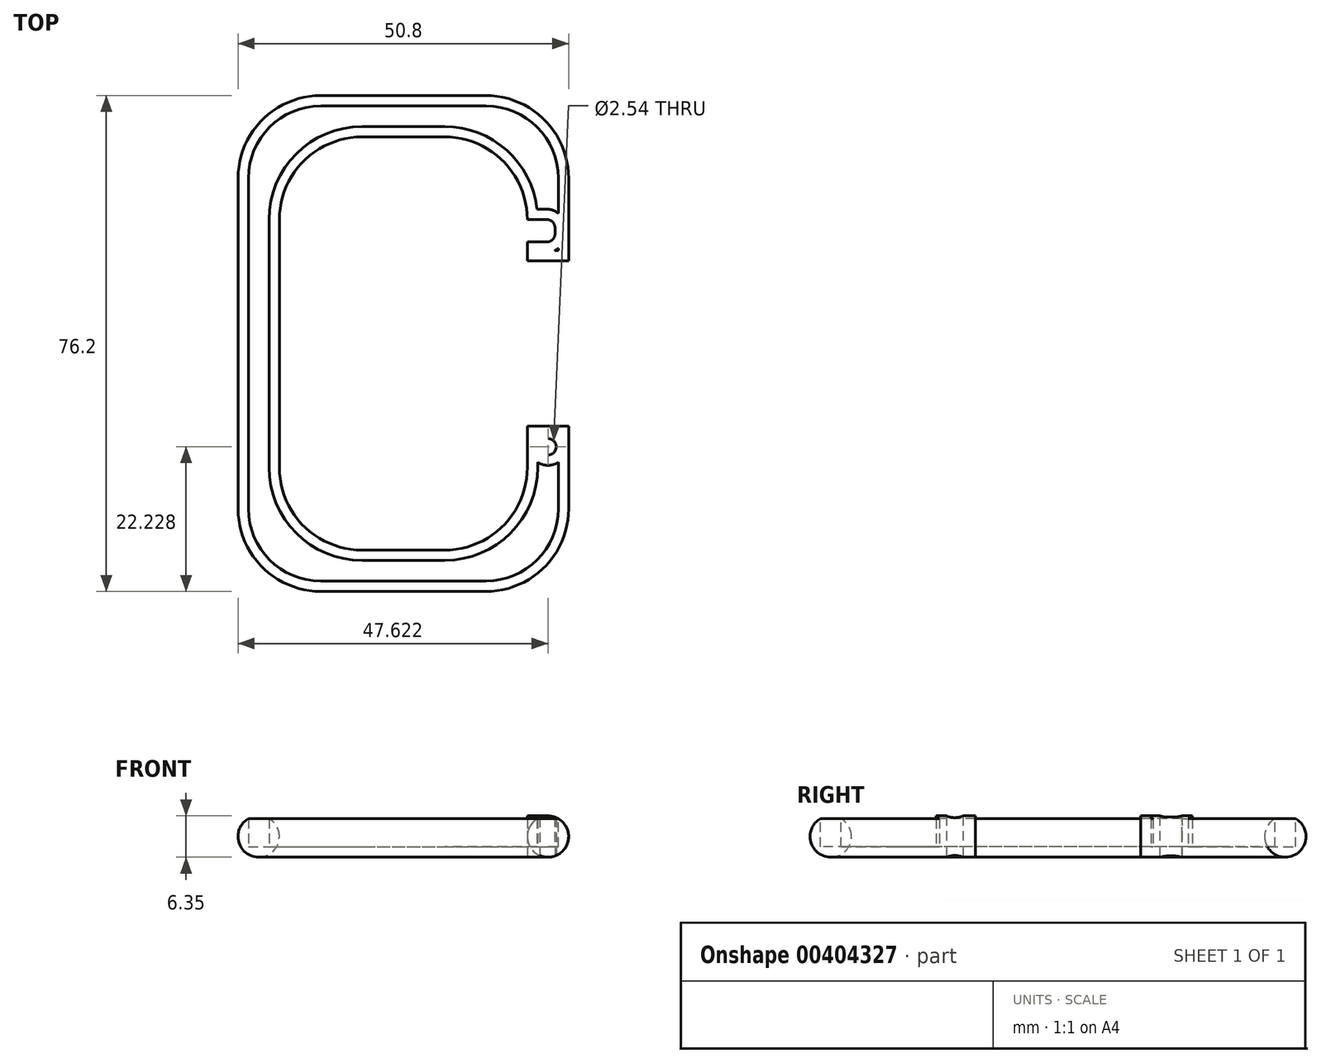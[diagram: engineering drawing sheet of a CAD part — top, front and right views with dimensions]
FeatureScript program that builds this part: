
annotation { "Feature Type Name" : "Feature", "Feature Type Description" : "" }
export const myFeature = defineFeature(function(context is Context, id is Id, definition is map)
    precondition{}
    {
        {
            var Q0;
            Q0=qCreatedBy(makeId("Top.planeOp"),FACE);
            var sketch = newSketch(context, id + "F0", { "sketchPlane" : qUnion([Q0])});
            skLineSegment(sketch, "E0.bottom", {"start": v(-121.23, 52.85) * mm, "end": v(-95.83, 52.85) * mm});
            skLineSegment(sketch, "E0.top", {"start": v(-114.88, 46.5) * mm, "end": v(-102.18, 46.5) * mm});
            skLineSegment(sketch, "E1.right", {"start": v(-127.58, 33.8) * mm, "end": v(-127.58, -4.3) * mm});
            skLineSegment(sketch, "E2.bottom", {"start": v(-114.88, -17) * mm, "end": v(-102.18, -17) * mm});
            skLineSegment(sketch, "E2.top", {"start": v(-121.23, -23.35) * mm, "end": v(-95.83, -23.35) * mm});
            skLineSegment(sketch, "E3.top", {"start": v(-83.13, 2.05) * mm, "end": v(-89.48, 2.05) * mm});
            skLineSegment(sketch, "E3.left", {"start": v(-83.13, -10.65) * mm, "end": v(-83.13, 2.05) * mm});
            skLineSegment(sketch, "E3.right", {"start": v(-89.48, -4.3) * mm, "end": v(-89.48, 2.05) * mm});
            skLineSegment(sketch, "E4.top", {"start": v(-83.13, 27.45) * mm, "end": v(-89.48, 27.45) * mm});
            skLineSegment(sketch, "E4.left", {"start": v(-83.13, 40.15) * mm, "end": v(-83.13, 27.45) * mm});
            skLineSegment(sketch, "E4.right", {"start": v(-89.48, 30.36) * mm, "end": v(-89.48, 27.45) * mm});
            skArc(sketch, "E5.filletArc", {"start": v(-127.58, -4.3) * mm, "mid": v(-123.86, -13.28) * mm, "end": v(-114.88, -17) * mm});
            skLineSegment(sketch, "E6", {"start": v(-133.93, 40.15) * mm, "end": v(-133.93, -10.65) * mm});
            skArc(sketch, "E7.filletArc", {"start": v(-133.93, -10.65) * mm, "mid": v(-130.21, -19.63) * mm, "end": v(-121.23, -23.35) * mm});
            skPoint(sketch, "E8.visualSharp", {"position": v(-127.58, 46.5) * mm});
            skArc(sketch, "E8.filletArc", {"start": v(-114.88, 46.5) * mm, "mid": v(-123.86, 42.78) * mm, "end": v(-127.58, 33.8) * mm});
            skArc(sketch, "E9.filletArc", {"start": v(-121.23, 52.85) * mm, "mid": v(-130.21, 49.13) * mm, "end": v(-133.93, 40.15) * mm});
            skPoint(sketch, "E10.visualSharp", {"position": v(-89.48, 46.5) * mm});
            skArc(sketch, "E10.filletArc", {"start": v(-89.48, 33.8) * mm, "mid": v(-93.2, 42.78) * mm, "end": v(-102.18, 46.5) * mm});
            skPoint(sketch, "E11.newPointB", {"position": v(-83.13, 46.5) * mm});
            skArc(sketch, "E11.filletArc", {"start": v(-83.13, 40.15) * mm, "mid": v(-86.85, 49.13) * mm, "end": v(-95.83, 52.85) * mm});
            skPoint(sketch, "E12.visualSharp", {"position": v(-89.48, -17) * mm});
            skArc(sketch, "E12.filletArc", {"start": v(-102.18, -17) * mm, "mid": v(-93.2, -13.28) * mm, "end": v(-89.48, -4.3) * mm});
            skArc(sketch, "E13.filletArc", {"start": v(-95.83, -23.35) * mm, "mid": v(-86.85, -19.63) * mm, "end": v(-83.13, -10.65) * mm});
            skCircle(sketch, "E14", {"center": v(-86.3, -1.12) * mm, "radius": 1.27 * mm});
            skLineSegment(sketch, "E15.bottom", {"start": v(-89.48, 33.8) * mm, "end": v(-86.5, 33.8) * mm});
            skLineSegment(sketch, "E15.top", {"start": v(-89.48, 30.36) * mm, "end": v(-86.5, 30.36) * mm});
            skLineSegment(sketch, "E15.right", {"start": v(-85.22, 32.53) * mm, "end": v(-85.22, 31.63) * mm});
            skPoint(sketch, "E16.visualSharp", {"position": v(-85.22, 30.36) * mm});
            skArc(sketch, "E16.filletArc", {"start": v(-86.5, 30.36) * mm, "mid": v(-85.6, 30.73) * mm, "end": v(-85.22, 31.63) * mm});
            skPoint(sketch, "E17.visualSharp", {"position": v(-85.22, 33.8) * mm});
            skArc(sketch, "E17.filletArc", {"start": v(-85.22, 32.53) * mm, "mid": v(-85.6, 33.43) * mm, "end": v(-86.5, 33.8) * mm});
            skSolve(sketch);
        }
        {
            var Q0;
            Q0=makeQuery(id+"F0.imprint","IMPRINT",FACE,{"disambiguationData":[TD([[makeQuery(id+"F0.imprint","IMPRINT",EDGE,{"derivedFrom":sQuery(id+"F0.wireOp",EDGE,"E0.bottom")}),-1.0]])]});
            extrude(context, id + "F1", {"entities" : qUnion([Q0]), "depth" : 6.35 * mm});
        }
        {
            var Q0;
            Q0=makeQuery(id+"F1.opExtrude","CAP_FACE",FACE,{"disambiguationData":[OSD([sQuery(id+"F0.wireOp",EDGE,"E0.bottom"),sQuery(id+"F0.wireOp",EDGE,"E0.top"),sQuery(id+"F0.wireOp",EDGE,"E1.right"),sQuery(id+"F0.wireOp",EDGE,"E2.bottom"),sQuery(id+"F0.wireOp",EDGE,"E2.top"),sQuery(id+"F0.wireOp",EDGE,"E3.top"),sQuery(id+"F0.wireOp",EDGE,"E3.left"),sQuery(id+"F0.wireOp",EDGE,"E3.right"),sQuery(id+"F0.wireOp",EDGE,"E4.top"),sQuery(id+"F0.wireOp",EDGE,"E4.left"),sQuery(id+"F0.wireOp",EDGE,"E4.right"),sQuery(id+"F0.wireOp",EDGE,"E5.filletArc"),sQuery(id+"F0.wireOp",EDGE,"E6"),sQuery(id+"F0.wireOp",EDGE,"E7.filletArc"),sQuery(id+"F0.wireOp",EDGE,"E8.filletArc"),sQuery(id+"F0.wireOp",EDGE,"E9.filletArc"),sQuery(id+"F0.wireOp",EDGE,"E10.filletArc"),sQuery(id+"F0.wireOp",EDGE,"E11.filletArc"),sQuery(id+"F0.wireOp",EDGE,"E12.filletArc"),sQuery(id+"F0.wireOp",EDGE,"E13.filletArc"),sQuery(id+"F0.wireOp",EDGE,"E14"),sQuery(id+"F0.wireOp",EDGE,"E15.bottom"),sQuery(id+"F0.wireOp",EDGE,"E15.top"),sQuery(id+"F0.wireOp",EDGE,"E15.right"),sQuery(id+"F0.wireOp",EDGE,"E16.filletArc"),sQuery(id+"F0.wireOp",EDGE,"E17.filletArc")])],"isStart":false});
            shell(context, id + "F2", {"entities" : qUnion([Q0]), "thickness" : 1.59 * mm});
        }
        {
            var Q0;
            Q0=makeQuery(id+"F1.opExtrude","CAP_EDGE",EDGE,{"disambiguationData":[OSD([sQuery(id+"F0.wireOp",EDGE,"E12.filletArc")])],"isStart":false});
            fillet(context, id + "F3", {"entities" : qUnion([Q0]), "radius" : 3.17 * mm, "tangentPropagation" : true, "allowEdgeOverflow" : false});
        }
        {
            var Q0;
            Q0=makeQuery(id+"F1.opExtrude","CAP_EDGE",EDGE,{"disambiguationData":[OSD([sQuery(id+"F0.wireOp",EDGE,"E4.left")])],"isStart":false});
            fillet(context, id + "F4", {"entities" : qUnion([Q0]), "radius" : 3.17 * mm, "tangentPropagation" : true, "allowEdgeOverflow" : false});
        }
        {
            var Q0;
            Q0=makeQuery(id+"F1.opExtrude","CAP_EDGE",EDGE,{"disambiguationData":[OSD([sQuery(id+"F0.wireOp",EDGE,"E1.right")])],"isStart":true});
            fillet(context, id + "F5", {"entities" : qUnion([Q0]), "radius" : 3.17 * mm, "tangentPropagation" : true, "allowEdgeOverflow" : false});
        }
        {
            var Q0;
            Q0=makeQuery(id+"F1.opExtrude","CAP_EDGE",EDGE,{"disambiguationData":[OSD([sQuery(id+"F0.wireOp",EDGE,"E6")])],"isStart":true});
            fillet(context, id + "F6", {"entities" : qUnion([Q0]), "radius" : 3.17 * mm, "tangentPropagation" : true, "allowEdgeOverflow" : false});
        }
    });
